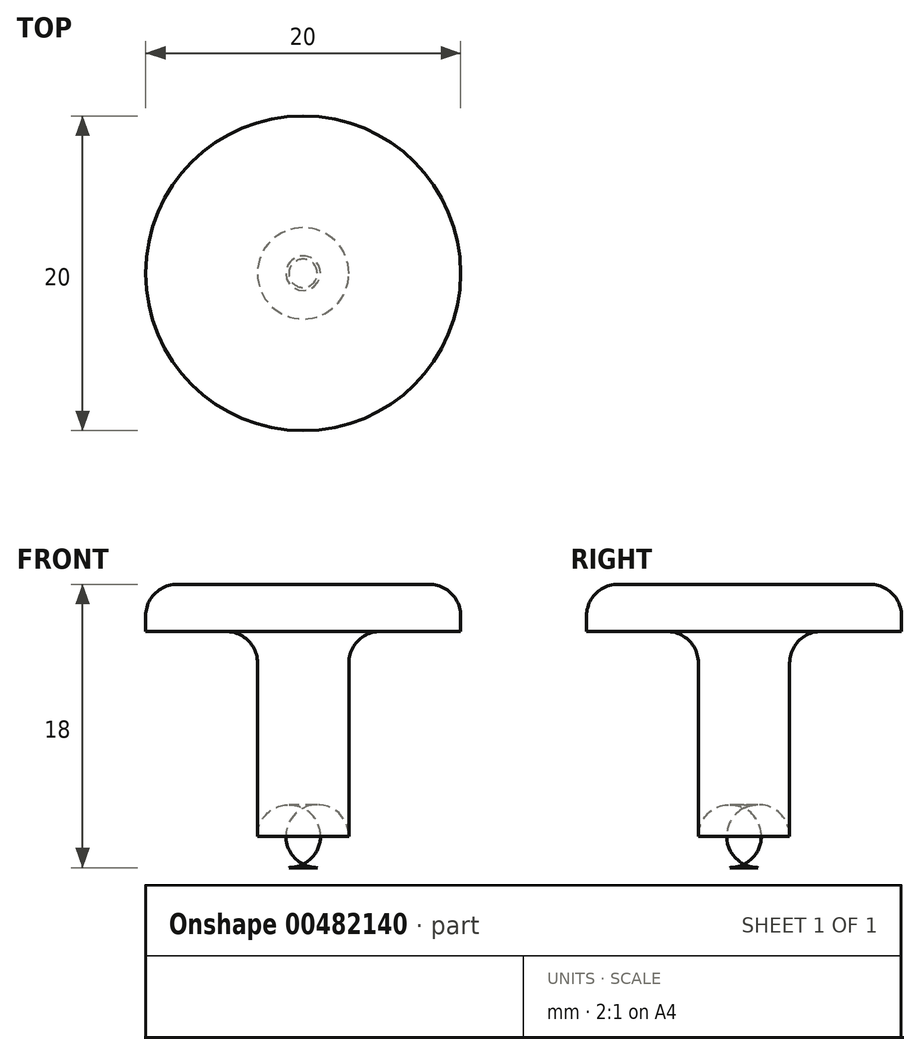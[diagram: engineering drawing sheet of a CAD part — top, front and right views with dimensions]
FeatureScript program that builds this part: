
annotation { "Feature Type Name" : "Feature", "Feature Type Description" : "" }
export const myFeature = defineFeature(function(context is Context, id is Id, definition is map)
    precondition{}
    {
        {
            var Q0;
            Q0=qCreatedBy(makeId("Front.planeOp"),FACE);
            var sketch = newSketch(context, id + "F0", { "sketchPlane" : qUnion([Q0])});
            skLineSegment(sketch, "E0.bottom", {"start": v(0, 0) * mm, "end": v(10, 0) * mm});
            skLineSegment(sketch, "E0.top", {"start": v(2.9, -3) * mm, "end": v(10, -3) * mm});
            skLineSegment(sketch, "E0.left", {"start": v(0, 0) * mm, "end": v(0, -3) * mm});
            skLineSegment(sketch, "E0.right", {"start": v(10, 0) * mm, "end": v(10, -3) * mm});
            skLineSegment(sketch, "E1.top", {"start": v(0, -18) * mm, "end": v(2.9, -18) * mm});
            skLineSegment(sketch, "E1.left", {"start": v(0, -3) * mm, "end": v(0, -18) * mm});
            skLineSegment(sketch, "E1.right", {"start": v(2.9, -3) * mm, "end": v(2.9, -18) * mm});
            skLineSegment(sketch, "E2", {"start": v(0, 5.54) * mm, "end": v(0, -28.1) * mm, "construction": true});
            skSolve(sketch);
        }
        {
            var Q0;
            Q0 = qSketchRegion(id + "F0", true);
            var Q1;
            Q1=sQuery(id+"F0.wireOp",EDGE,"E2");
            revolve(context, id + "F1", {"entities" : qUnion([Q0]), "axis" : qUnion([Q1]), "revolveType" : RevolveType.FULL});
        }
        {
            var Q0;
            Q0=makeQuery(id+"F1.opRevolve","SWEPT_EDGE",EDGE,{"disambiguationData":[OSD([sQuery(id+"F0.wireOp",EDGE,"E1.top"),sQuery(id+"F0.wireOp",EDGE,"E1.right")])]});
            var Q1;
            Q1=makeQuery(id+"F1.opRevolve","SWEPT_EDGE",EDGE,{"disambiguationData":[OSD([sQuery(id+"F0.wireOp",EDGE,"E0.bottom"),sQuery(id+"F0.wireOp",EDGE,"E0.right")])]});
            var Q2;
            Q2=makeQuery(id+"F1.opRevolve","SWEPT_FACE",FACE,{"disambiguationData":[OSD([sQuery(id+"F0.wireOp",EDGE,"E1.right")])]});
            fillet(context, id + "F2", {"entities" : qUnion([Q0, Q1, Q2]), "radius" : 2 * mm, "tangentPropagation" : true, "allowEdgeOverflow" : false});
        }
    });
